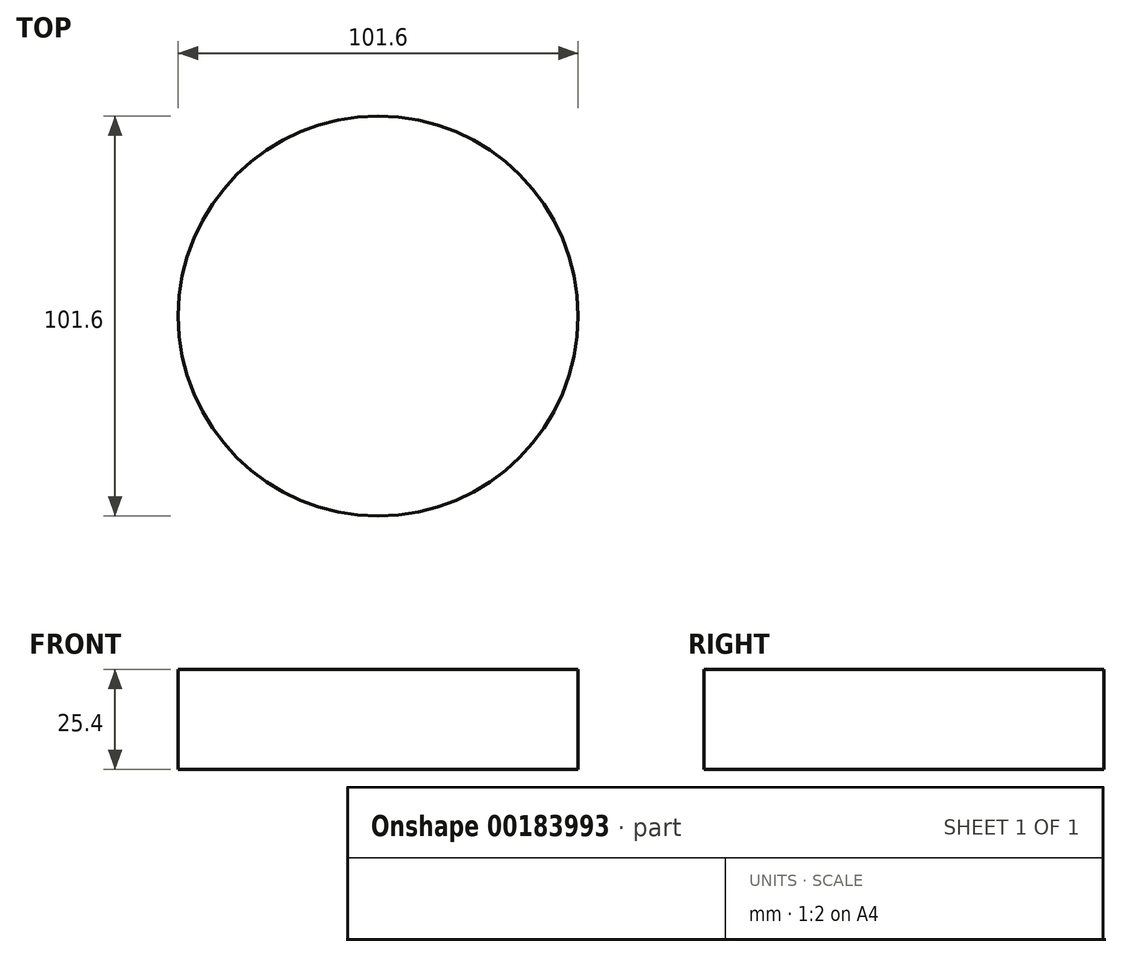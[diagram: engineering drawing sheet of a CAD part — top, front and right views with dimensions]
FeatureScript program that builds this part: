
annotation { "Feature Type Name" : "Feature", "Feature Type Description" : "" }
export const myFeature = defineFeature(function(context is Context, id is Id, definition is map)
    precondition{}
    {
        {
            var Q0;
            Q0=qCreatedBy(makeId("Top.planeOp"),FACE);
            var sketch = newSketch(context, id + "F0", { "sketchPlane" : qUnion([Q0])});
            skCircle(sketch, "E0", {"center": v(0, 0) * mm, "radius": 50.8 * mm});
            skSolve(sketch);
        }
        {
            var Q0;
            Q0 = qSketchRegion(id + "F0", true);
            extrude(context, id + "F1", {"entities" : qUnion([Q0]), "depth" : 25.4 * mm});
        }
    });
